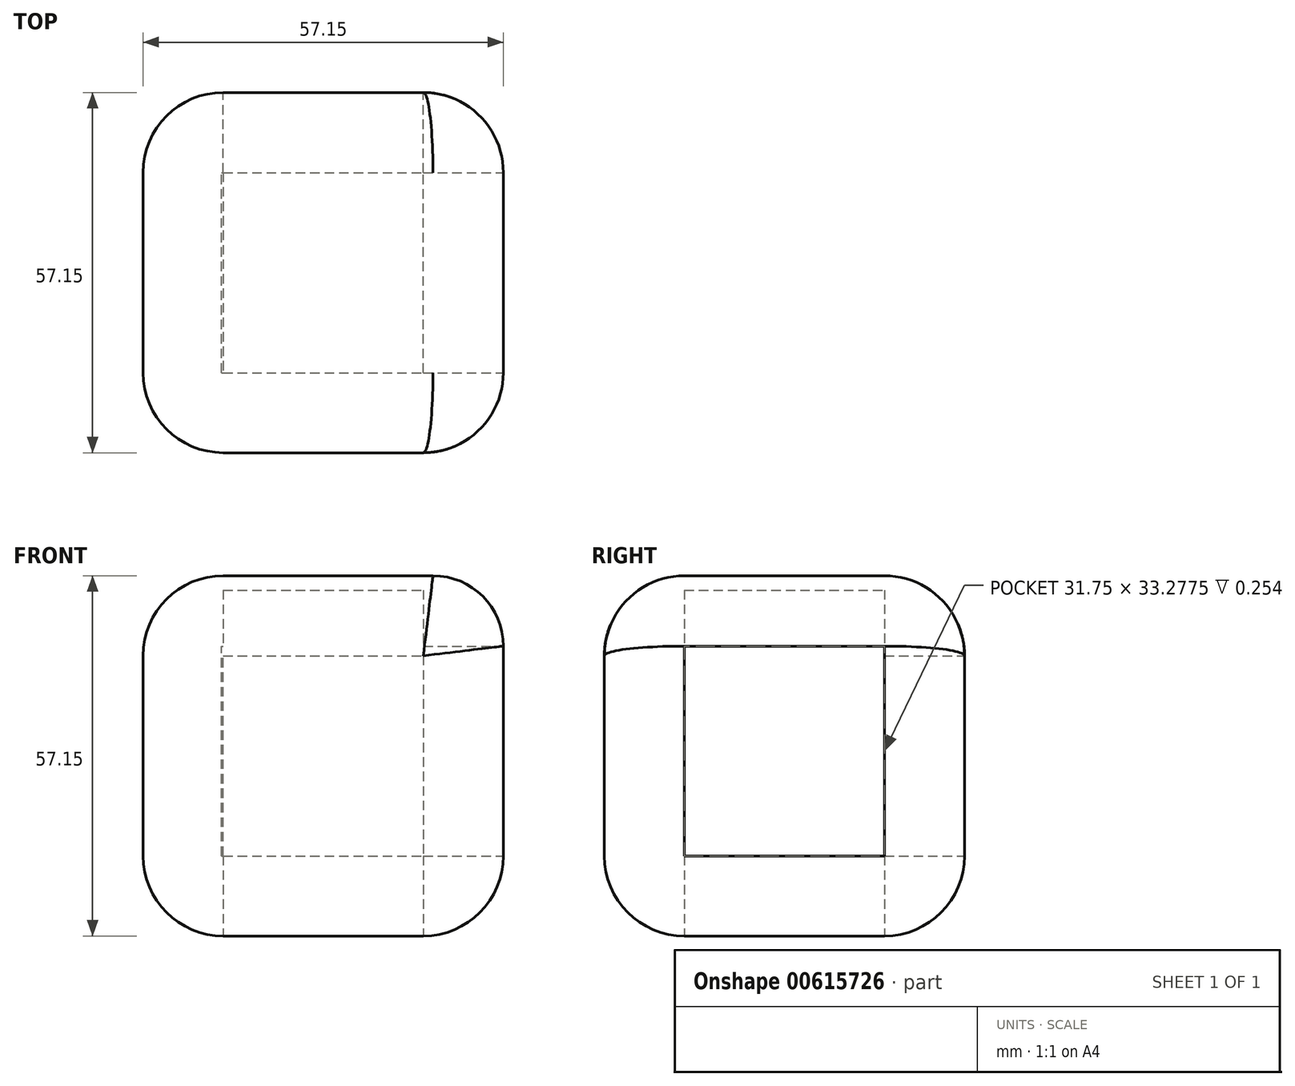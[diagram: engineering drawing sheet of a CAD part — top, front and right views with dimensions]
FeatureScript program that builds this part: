
annotation { "Feature Type Name" : "Feature", "Feature Type Description" : "" }
export const myFeature = defineFeature(function(context is Context, id is Id, definition is map)
    precondition{}
    {
        {
            var Q0;
            Q0=qCreatedBy(makeId("Front.planeOp"),FACE);
            var sketch = newSketch(context, id + "F0", { "sketchPlane" : qUnion([Q0])});
            skLineSegment(sketch, "E0.bottom", {"start": v(0, 0) * mm, "end": v(57.15, 0) * mm});
            skLineSegment(sketch, "E0.top", {"start": v(0, 57.15) * mm, "end": v(45.98, 57.15) * mm});
            skLineSegment(sketch, "E0.left", {"start": v(0, 0) * mm, "end": v(0, 57.15) * mm});
            skLineSegment(sketch, "E0.right", {"start": v(57.15, 0) * mm, "end": v(57.15, 45.98) * mm});
            skArc(sketch, "E1", {"start": v(57.15, 45.98) * mm, "mid": v(53.77, 53.98) * mm, "end": v(45.67, 57.15) * mm});
            skPoint(sketch, "E2", {"position": v(45.67, 57.15) * mm});
            skPoint(sketch, "E3", {"position": v(57.15, 45.81) * mm});
            skSolve(sketch);
        }
        {
            var Q0;
            Q0=makeQuery(id+"F0.imprint","IMPRINT",FACE,{"disambiguationData":[TD([[makeQuery(id+"F0.imprint","IMPRINT",EDGE,{"derivedFrom":sQuery(id+"F0.wireOp",EDGE,"E0.bottom")}),1.0]])]});
            extrude(context, id + "F1", {"entities" : qUnion([Q0]), "depth" : 57.15 * mm, "offsetDistance" : 25.4 * mm});
        }
        {
            var Q0;
            Q0=makeQuery(id+"F1.opExtrude","CAP_EDGE",EDGE,{"disambiguationData":[OSD([sQuery(id+"F0.wireOp",EDGE,"E0.right")])],"isStart":true});
            var Q1;
            Q1=makeQuery(id+"F1.opExtrude","CAP_EDGE",EDGE,{"disambiguationData":[OSD([sQuery(id+"F0.wireOp",EDGE,"E0.right")])],"isStart":false});
            var Q2;
            Q2=makeQuery(id+"F1.opExtrude","CAP_EDGE",EDGE,{"disambiguationData":[OSD([sQuery(id+"F0.wireOp",EDGE,"E0.left")])],"isStart":true});
            var Q3;
            Q3=makeQuery(id+"F1.opExtrude","CAP_EDGE",EDGE,{"disambiguationData":[OSD([sQuery(id+"F0.wireOp",EDGE,"E0.left")])],"isStart":false});
            var Q4;
            Q4=makeQuery(id+"F1.opExtrude","SWEPT_EDGE",EDGE,{"disambiguationData":[OSD([sQuery(id+"F0.wireOp",EDGE,"E0.top"),sQuery(id+"F0.wireOp",EDGE,"E0.left")])]});
            var Q5;
            Q5=makeQuery(id+"F1.opExtrude","SWEPT_EDGE",EDGE,{"disambiguationData":[OSD([sQuery(id+"F0.wireOp",EDGE,"E0.bottom"),sQuery(id+"F0.wireOp",EDGE,"E0.left")])]});
            var Q6;
            Q6=makeQuery(id+"F1.opExtrude","CAP_EDGE",EDGE,{"disambiguationData":[OSD([sQuery(id+"F0.wireOp",EDGE,"E0.bottom")])],"isStart":false});
            var Q7;
            Q7=makeQuery(id+"F1.opExtrude","CAP_EDGE",EDGE,{"disambiguationData":[OSD([sQuery(id+"F0.wireOp",EDGE,"E0.bottom")])],"isStart":true});
            var Q8;
            Q8=makeQuery(id+"F1.opExtrude","SWEPT_EDGE",EDGE,{"disambiguationData":[OSD([sQuery(id+"F0.wireOp",EDGE,"E0.bottom"),sQuery(id+"F0.wireOp",EDGE,"E0.right")])]});
            fillet(context, id + "F2", {"entities" : qUnion([Q0, Q1, Q2, Q3, Q4, Q5, Q6, Q7, Q8]), "radius" : 12.7 * mm, "tangentPropagation" : true, "allowEdgeOverflow" : false});
        }
        {
            var Q0;
            Q0=makeQuery(id+"F1.opExtrude","SWEPT_FACE",FACE,{"disambiguationData":[OSD([sQuery(id+"F0.wireOp",EDGE,"E0.bottom")])]});
            extrude(context, id + "F3", {"entities" : qUnion([Q0]), "operationType" : NewBodyOperationType.REMOVE, "oppositeDirection" : true, "depth" : 54.86 * mm, "offsetDistance" : 25.4 * mm});
        }
        {
            var Q0;
            Q0=makeQuery(id+"F1.opExtrude","SWEPT_FACE",FACE,{"disambiguationData":[OSD([sQuery(id+"F0.wireOp",EDGE,"E0.right")])]});
            extrude(context, id + "F4", {"entities" : qUnion([Q0]), "operationType" : NewBodyOperationType.REMOVE, "oppositeDirection" : true, "depth" : 44.7 * mm, "offsetDistance" : 25.4 * mm});
        }
        {
            var Q0;
            Q0=makeQuery(id+"F1.opExtrude","CAP_FACE",FACE,{"disambiguationData":[OSD([sQuery(id+"F0.wireOp",EDGE,"E0.bottom"),sQuery(id+"F0.wireOp",EDGE,"E0.top"),sQuery(id+"F0.wireOp",EDGE,"E0.left"),sQuery(id+"F0.wireOp",EDGE,"E0.right"),sQuery(id+"F0.wireOp",EDGE,"E1")])],"isStart":true});
            extrude(context, id + "F5", {"entities" : qUnion([Q0]), "operationType" : NewBodyOperationType.REMOVE, "oppositeDirection" : true, "depth" : 25.4 * mm, "offsetDistance" : 25.4 * mm});
        }
    });
